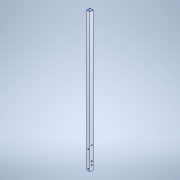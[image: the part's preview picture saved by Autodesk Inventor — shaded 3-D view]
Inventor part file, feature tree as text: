
AUTODESK INVENTOR PART (.ipt)
format: ipt  version: 2020.3 (Build 243373000, 373)  size: 152,576 bytes
history: native  units: mm
features: sketch x5, hole x3, extrude x2, other x1
ambient origin geometry x8: Origin, YZ Plane, XZ Plane, XY Plane, X Axis, Y Axis, Z Axis, Center Point
bodies: Body1 (feature_tree)
feature tree (11):
  other  "ソリッド1"
  extrude  "押し出し1"  Depth=9.0mm
  hole  "穴1"  [1 undecoded]
  hole  "穴2"  [1 undecoded]
  hole  "穴3"  [1 undecoded]
  extrude  "押し出し2"  Depth=1.2mm
  sketch  "スケッチ1"
  sketch  "スケッチ2"
  sketch  "スケッチ3"
  sketch  "スケッチ4"
  sketch  "スケッチ5"
note: 3 required parameter values undecoded (feature->parameter linkage not recoverable at this tier; creation-order binding heuristic only, values carry confidence <= 0.55)
